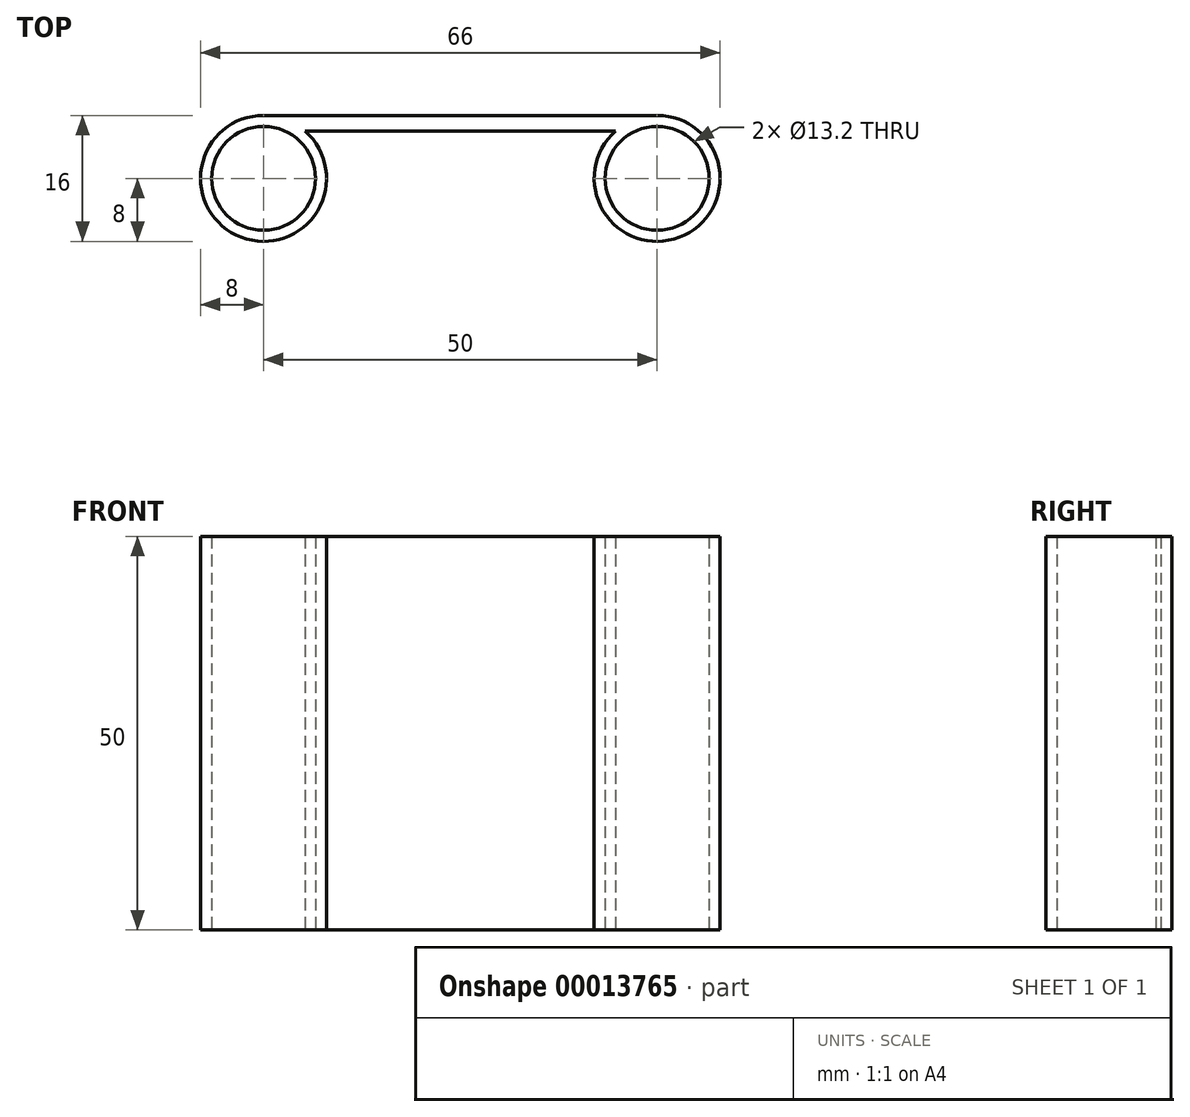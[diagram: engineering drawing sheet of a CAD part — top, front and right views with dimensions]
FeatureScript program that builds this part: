
annotation { "Feature Type Name" : "Feature", "Feature Type Description" : "" }
export const myFeature = defineFeature(function(context is Context, id is Id, definition is map)
    precondition{}
    {
        {
            var Q0;
            Q0=qCreatedBy(makeId("Top.planeOp"),FACE);
            var sketch = newSketch(context, id + "F0", { "sketchPlane" : qUnion([Q0])});
            skCircle(sketch, "E0", {"center": v(-25, 0) * mm, "radius": 6.6 * mm});
            skCircle(sketch, "E1", {"center": v(-25, 0) * mm, "radius": 8 * mm});
            skCircle(sketch, "E2.MirrorC", {"center": v(25, 0) * mm, "radius": 8 * mm});
            skCircle(sketch, "E3.MirrorC", {"center": v(25, 0) * mm, "radius": 6.6 * mm});
            skLineSegment(sketch, "E4", {"start": v(-25, 8) * mm, "end": v(25, 8) * mm});
            skLineSegment(sketch, "E5", {"start": v(-19.7, 6) * mm, "end": v(19.7, 6) * mm});
            skSolve(sketch);
        }
        {
            var Q0;
            Q0 = qSketchRegion(id + "F0", true);
            extrude(context, id + "F1", {"entities" : qUnion([Q0]), "depth" : 50 * mm});
        }
    });
